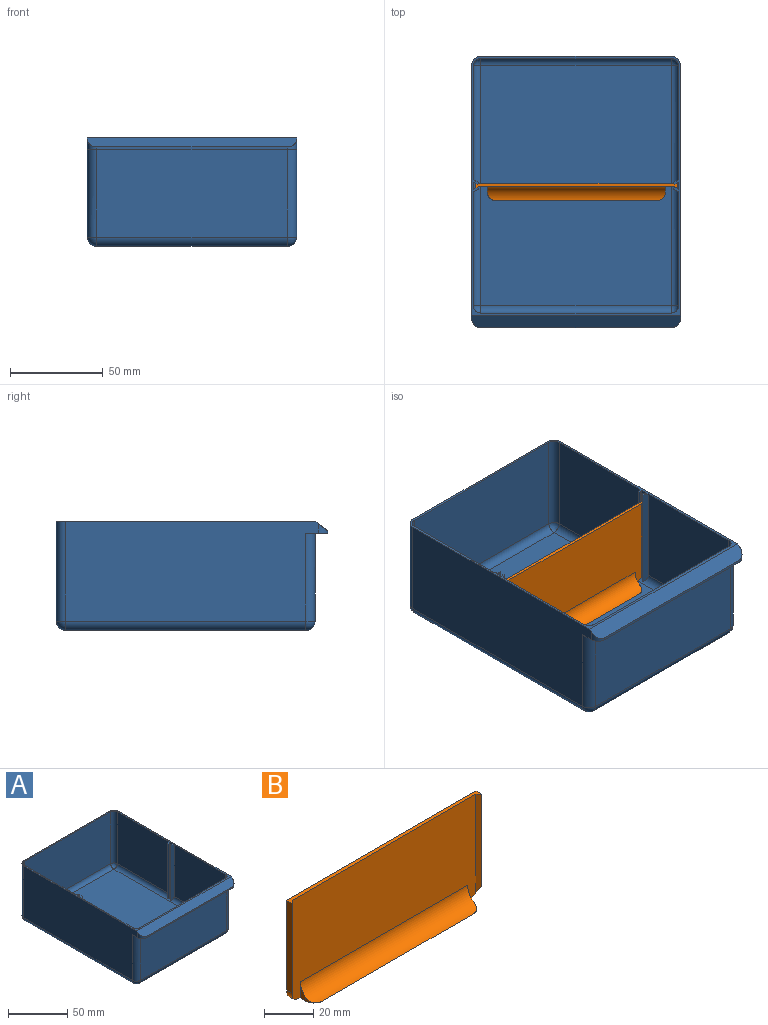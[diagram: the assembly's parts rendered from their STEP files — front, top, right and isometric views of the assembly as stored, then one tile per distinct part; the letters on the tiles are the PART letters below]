
ASSEMBLY  parts=2 mates=1
PART A: 63 faces, bbox 112.8x146.3x58.7 mm
  f0: plane 112.8x11.78mm, normal (0,0,-1), area 138.7mm2, adj f2,f3,f11,f12,f52,f54,f55,f57
  f1: plane 102.8x52.6mm, normal (0,-1,0), area 5407.3mm2, adj f2,f3,f22,f56
  f2: cylinder r=5mm len=52.6mm, axis (0,0,-1), area 395.4mm2, adj f0,f1,f12,f20,f56,f58
  f3: cylinder r=5mm len=52.6mm, axis (0,0,1), area 395.4mm2, adj f0,f1,f11,f24,f56,f57
  f4: plane 61.5x53.7mm, normal (-1,0,0), area 3302.7mm2, adj f5,f10,f30,f49
  f5: cylinder r=3.9mm len=129.5mm, axis (0,1,0), area 781.9mm2, adj f4,f6,f27,f29,f31,f35,f46,f47
  f6: plane 53.7x3.95mm, normal (-1,0,0), area 212.2mm2, adj f5,f10,f48,f50
  f7: plane 61.5x53.7mm, normal (1,0,0), area 3302.7mm2, adj f9,f10,f34,f45
  f8: plane 53.7x3.95mm, normal (1,0,0), area 212.2mm2, adj f9,f10,f40,f44
  f9: cylinder r=3.9mm len=129.5mm, axis (0,-1,0), area 781.9mm2, adj f7,f8,f25,f29,f36,f38,f40,f41
  f10: plane 139.93x112.8mm, normal (0,0,1), area 612.5mm2, adj f4,f6,f7,f8,f11,f12,f13,f15
  f11: plane 136.28x53.7mm, normal (-1,0,0), area 6996.5mm2, adj f0,f3,f10,f19,f23,f53,f54
  f12: plane 136.28x53.7mm, normal (1,0,0), area 6996.5mm2, adj f0,f2,f10,f15,f17,f53,f55
  f13: plane 102.8x53.7mm, normal (0,1,0), area 5520.4mm2, adj f10,f15,f18,f19
  f14: plane 129.5x102.8mm, normal (0,0,-1), area 13312.6mm2, adj f17,f18,f22,f23
  f15: cylinder r=5mm len=53.7mm, axis (0,0,1), area 421.8mm2, adj f10,f12,f13,f16
  f16: sphere r=5mm, area 39.3mm2, adj f15,f17,f18
  f17: cylinder r=5mm len=129.5mm, axis (0,1,0), area 1017.1mm2, adj f12,f14,f16,f20
  f18: cylinder r=5mm len=102.8mm, axis (-1,0,0), area 807.4mm2, adj f13,f14,f16,f21
  f19: cylinder r=5mm len=53.7mm, axis (0,0,-1), area 421.8mm2, adj f10,f11,f13,f21
  f20: sphere r=5mm, area 39.3mm2, adj f2,f17,f22
  f21: sphere r=5mm, area 39.3mm2, adj f18,f19,f23
  f22: cylinder r=5mm len=102.8mm, axis (1,0,0), area 807.4mm2, adj f1,f14,f20,f24
  f23: cylinder r=5mm len=129.5mm, axis (0,-1,0), area 1017.1mm2, adj f11,f14,f21,f24
  f24: sphere r=5mm, area 39.3mm2, adj f3,f22,f23
  f25: plane 61.5x53.7mm, normal (1,0,0), area 3302.7mm2, adj f9,f10,f39,f42
  f26: plane 102.8x53.7mm, normal (0,1,0), area 5520.4mm2, adj f10,f32,f37,f39
  f27: plane 61.5x53.7mm, normal (-1,0,0), area 3302.7mm2, adj f5,f10,f32,f46
  f28: plane 102.8x53.7mm, normal (0,-1,0), area 5520.4mm2, adj f10,f30,f33,f34
  f29: plane 129.5x102.8mm, normal (0,0,1), area 13312.6mm2, adj f5,f9,f33,f37
  f30: cylinder r=3.9mm len=53.7mm, axis (0,0,1), area 329mm2, adj f4,f10,f28,f31
  f31: sphere r=3.9mm, area 23.9mm2, adj f5,f30,f33
  f32: cylinder r=3.9mm len=53.7mm, axis (0,0,-1), area 329mm2, adj f10,f26,f27,f35
  f33: cylinder r=3.9mm len=102.8mm, axis (-1,0,0), area 629.8mm2, adj f28,f29,f31,f36
  f34: cylinder r=3.9mm len=53.7mm, axis (0,0,-1), area 329mm2, adj f7,f10,f28,f36
  f35: sphere r=3.9mm, area 23.9mm2, adj f5,f32,f37
  f36: sphere r=3.9mm, area 23.9mm2, adj f9,f33,f34
  f37: cylinder r=3.9mm len=102.8mm, axis (1,0,0), area 629.8mm2, adj f26,f29,f35,f38
  f38: sphere r=3.9mm, area 23.9mm2, adj f9,f37,f39
  f39: cylinder r=3.9mm len=53.7mm, axis (0,0,1), area 329mm2, adj f10,f25,f26,f38
  f40: plane 57.13x2.05mm, normal (-0.5,0.87,0), area 132.8mm2, adj f8,f9,f10,f41
  f41: plane 57.39x0.97mm, normal (0.87,0.5,0), area 63mm2, adj f9,f10,f40,f42
  f42: plane 57.38x2.6mm, normal (0.5,-0.87,0), area 169.1mm2, adj f9,f10,f25,f41
  f43: plane 57.39x0.97mm, normal (0.87,-0.5,0), area 63mm2, adj f9,f10,f44,f45
  f44: plane 57.13x2.05mm, normal (-0.5,-0.87,0), area 132.8mm2, adj f8,f9,f10,f43
  f45: plane 57.38x2.6mm, normal (0.5,0.87,0), area 169.1mm2, adj f7,f9,f10,f43
  f46: plane 57.38x2.6mm, normal (-0.5,-0.87,0), area 169.1mm2, adj f5,f10,f27,f47
  f47: plane 57.39x0.97mm, normal (-0.87,0.5,0), area 63mm2, adj f5,f10,f46,f48
  f48: plane 57.13x2.05mm, normal (0.5,0.87,0), area 132.8mm2, adj f5,f6,f10,f47
  f49: plane 57.38x2.6mm, normal (-0.5,0.87,0), area 169.1mm2, adj f4,f5,f10,f51
  f50: plane 57.13x2.05mm, normal (0.5,-0.87,0), area 132.8mm2, adj f5,f6,f10,f51
  f51: plane 57.39x0.97mm, normal (-0.87,-0.5,0), area 63mm2, adj f5,f10,f49,f50
  f52: plane 102.8x1.35mm, normal (0,-1,0), area 138.8mm2, adj f0,f53,f54,f55
  f53: plane 112.8x6.35mm, normal (0,-0.62,0.79), area 898mm2, adj f10,f11,f12,f52,f54,f55
  f54: cylinder r=5mm len=5.29mm, axis (0,0,-1), area 21.8mm2, adj f0,f11,f52,f53
  f55: cylinder r=5mm len=5.29mm, axis (0,0,1), area 21.8mm2, adj f0,f12,f52,f53
  f56: plane 110.6x1.92mm, normal (0,0,-1), area 9.5mm2, adj f1,f2,f3,f57,f58,f60
  f57: plane 5.25x3.65mm, normal (1,0,0), area 18mm2, adj f0,f3,f56,f60,f61
  f58: plane 5.25x3.65mm, normal (-1,0,0), area 18mm2, adj f0,f2,f56,f60,f62
  f59: plane 102.8x0.82mm, normal (0,1,0), area 83.9mm2, adj f0,f60,f61,f62
  f60: plane 110.6x5.63mm, normal (0,0.62,-0.79), area 784.4mm2, adj f56,f57,f58,f59,f61,f62
  f61: cylinder r=3.9mm len=3.9mm, axis (0,0,-1), area 11.8mm2, adj f0,f57,f59,f60
  f62: cylinder r=3.9mm len=3.9mm, axis (0,0,1), area 11.8mm2, adj f0,f58,f59,f60
PART B: 15 faces, bbox 109.5x10.3x51.6 mm
  f0: plane 7.94x3.18mm, normal (-1,0,0), area 11.1mm2, adj f1,f3,f4,f13
  f1: plane 96.04x9.53mm, normal (0,0,-1), area 905.1mm2, adj f0,f2,f3,f8,f11,f12,f13,f14
  f2: plane 7.94x3.18mm, normal (1,0,0), area 11.1mm2, adj f1,f3,f4,f14
  f3: cylinder r=7.94mm len=96.04mm, axis (1,0,0), area 1173.2mm2, adj f0,f1,f2,f4,f13,f14
  f4: plane 105.57x50.8mm, normal (0,-1,0), area 4594.3mm2, adj f0,f2,f3,f7,f9,f10,f11,f12
  f5: plane 44.45x3.18mm, normal (-1,0,0), area 141.1mm2, adj f7,f8,f9,f11
  f6: plane 44.45x3.18mm, normal (1,0,0), area 141.1mm2, adj f7,f8,f10,f12
  f7: plane 108.74x3.18mm, normal (0,0,1), area 175.2mm2, adj f4,f5,f6,f8,f9,f10
  f8: plane 108.74x50.8mm, normal (0,1,0), area 5506.9mm2, adj f1,f5,f6,f7,f11,f12
  f9: plane 49.42x2.35mm, normal (0.71,-0.71,0), area 106.3mm2, adj f4,f5,f7,f11
  f10: plane 49.42x2.35mm, normal (-0.71,-0.71,0), area 106.3mm2, adj f4,f6,f7,f12
  f11: cylinder r=6.35mm len=6.35mm, axis (0,-1,0), area 19.5mm2, adj f1,f4,f5,f8,f9
  f12: cylinder r=6.35mm len=6.35mm, axis (0,1,0), area 19.5mm2, adj f1,f4,f6,f8,f10
  f13: cylinder r=4.76mm len=4.76mm, axis (0,0,-1), area 5.9mm2, adj f0,f1,f3
  f14: cylinder r=4.76mm len=4.76mm, axis (0,0,-1), area 5.9mm2, adj f1,f2,f3
PLACE A t=(0,0,-0.01)mm
PLACE B t=(2.26,71.16,1.09)mm
MATE planar B.f1 <-> A.f29  axis (0,0,-1) through (56.63,66.43,1.09)mm
